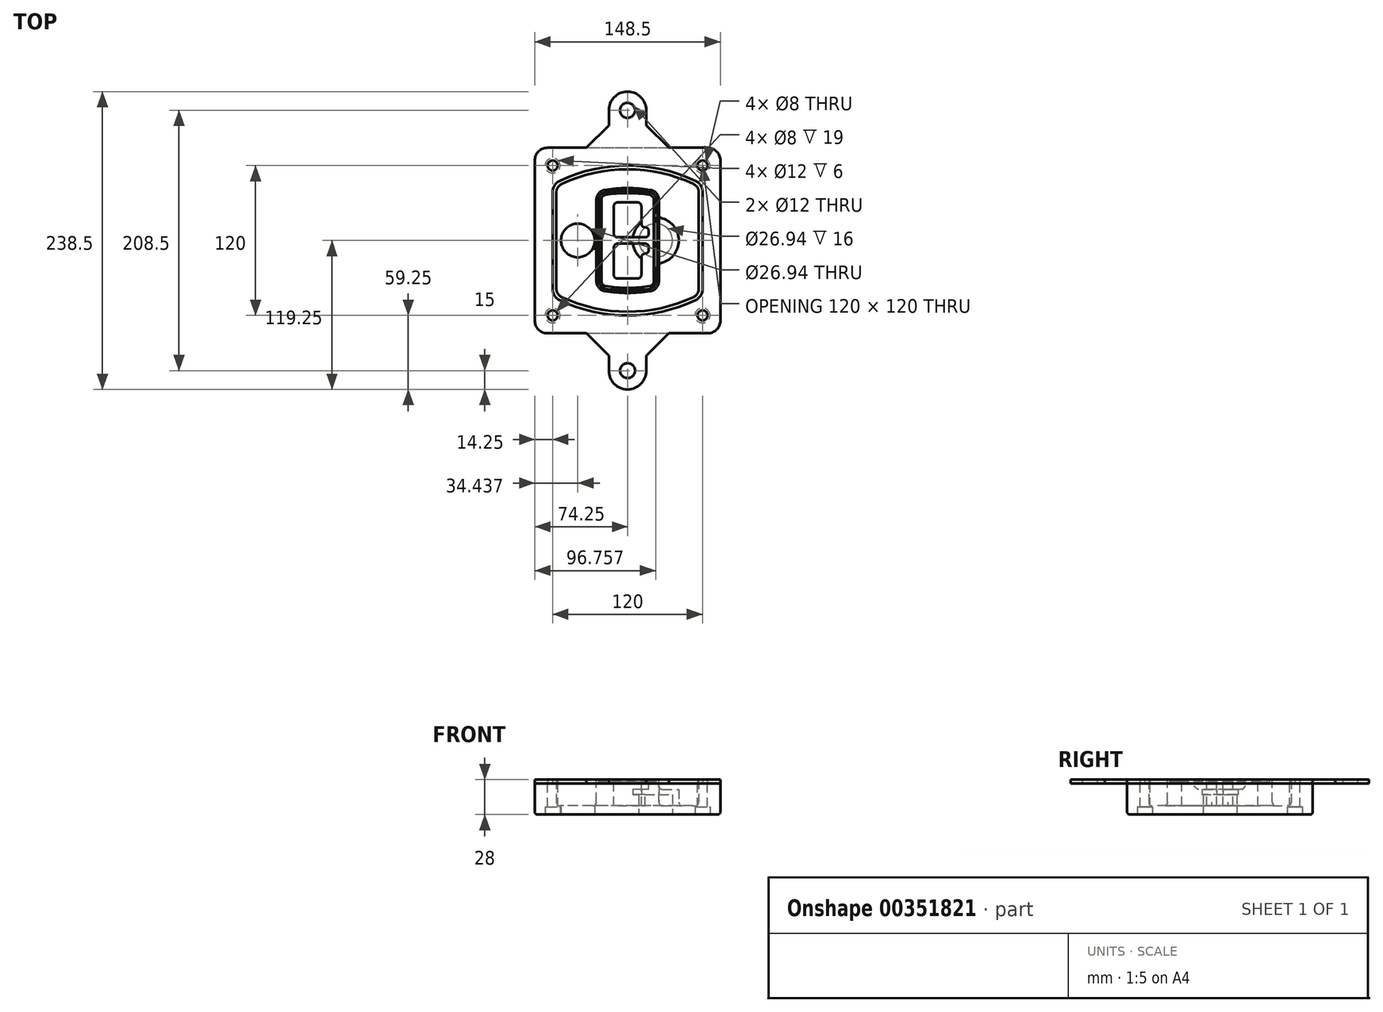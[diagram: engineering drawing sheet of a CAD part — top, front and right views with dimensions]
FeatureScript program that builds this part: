
annotation { "Feature Type Name" : "Feature", "Feature Type Description" : "" }
export const myFeature = defineFeature(function(context is Context, id is Id, definition is map)
    precondition{}
    {
        {
            var Q0;
            Q0=qCreatedBy(makeId("Top.planeOp"),FACE);
            var sketch = newSketch(context, id + "F0", { "sketchPlane" : qUnion([Q0])});
            skPoint(sketch, "E0.rect.middle", {"position": v(0, 0) * mm});
            skLineSegment(sketch, "E1.bottom", {"start": v(-64.25, -74.25) * mm, "end": v(64.25, -74.25) * mm});
            skLineSegment(sketch, "E1.top", {"start": v(-64.25, 74.25) * mm, "end": v(64.25, 74.25) * mm});
            skLineSegment(sketch, "E1.left", {"start": v(-74.25, -64.25) * mm, "end": v(-74.25, 64.25) * mm});
            skLineSegment(sketch, "E1.right", {"start": v(74.25, -64.25) * mm, "end": v(74.25, 64.25) * mm});
            skLineSegment(sketch, "E2", {"start": v(-74.25, 74.25) * mm, "end": v(74.25, -74.25) * mm, "construction": true});
            skLineSegment(sketch, "E3", {"start": v(74.25, 74.25) * mm, "end": v(-74.25, -74.25) * mm, "construction": true});
            skCircle(sketch, "E4", {"center": v(-60, 60) * mm, "radius": 4 * mm});
            skCircle(sketch, "E5", {"center": v(60, 60) * mm, "radius": 4 * mm});
            skCircle(sketch, "E6", {"center": v(60, -60) * mm, "radius": 4 * mm});
            skCircle(sketch, "E7", {"center": v(-60, -60) * mm, "radius": 4 * mm});
            skLineSegment(sketch, "E8", {"start": v(-60, 60) * mm, "end": v(60, 60) * mm, "construction": true});
            skLineSegment(sketch, "E9", {"start": v(60, 60) * mm, "end": v(60, -60) * mm, "construction": true});
            skLineSegment(sketch, "E10", {"start": v(60, -60) * mm, "end": v(-60, -60) * mm, "construction": true});
            skLineSegment(sketch, "E11", {"start": v(-60, -60) * mm, "end": v(-60, 60) * mm, "construction": true});
            skLineSegment(sketch, "E12", {"start": v(-60, 38.83) * mm, "end": v(-60, -38.83) * mm});
            skLineSegment(sketch, "E13", {"start": v(60, 38.83) * mm, "end": v(60, -38.83) * mm});
            skArc(sketch, "E14", {"start": v(54.26, 47.88) * mm, "mid": v(0, 60) * mm, "end": v(-54.26, 47.88) * mm});
            skArc(sketch, "E15", {"start": v(-54.26, -47.88) * mm, "mid": v(0, -60) * mm, "end": v(54.26, -47.88) * mm});
            skLineSegment(sketch, "E16", {"start": v(-60, 0) * mm, "end": v(60, 0) * mm, "construction": true});
            skPoint(sketch, "E17.visualSharp", {"position": v(-60, -45) * mm});
            skArc(sketch, "E17.filletArc", {"start": v(-60, -38.83) * mm, "mid": v(-58.44, -44.2) * mm, "end": v(-54.26, -47.88) * mm});
            skPoint(sketch, "E18.visualSharp", {"position": v(-60, 45) * mm});
            skArc(sketch, "E18.filletArc", {"start": v(-54.26, 47.88) * mm, "mid": v(-58.44, 44.2) * mm, "end": v(-60, 38.83) * mm});
            skPoint(sketch, "E19.visualSharp", {"position": v(60, 45) * mm});
            skArc(sketch, "E19.filletArc", {"start": v(60, 38.83) * mm, "mid": v(58.44, 44.2) * mm, "end": v(54.26, 47.88) * mm});
            skPoint(sketch, "E20.visualSharp", {"position": v(60, -45) * mm});
            skArc(sketch, "E20.filletArc", {"start": v(54.26, -47.88) * mm, "mid": v(58.44, -44.2) * mm, "end": v(60, -38.83) * mm});
            skPoint(sketch, "E21.visualSharp", {"position": v(-74.25, 74.25) * mm});
            skArc(sketch, "E21.filletArc", {"start": v(-64.25, 74.25) * mm, "mid": v(-71.32, 71.32) * mm, "end": v(-74.25, 64.25) * mm});
            skPoint(sketch, "E22.visualSharp", {"position": v(74.25, 74.25) * mm});
            skArc(sketch, "E22.filletArc", {"start": v(74.25, 64.25) * mm, "mid": v(71.32, 71.32) * mm, "end": v(64.25, 74.25) * mm});
            skPoint(sketch, "E23.visualSharp", {"position": v(74.25, -74.25) * mm});
            skArc(sketch, "E23.filletArc", {"start": v(64.25, -74.25) * mm, "mid": v(71.32, -71.32) * mm, "end": v(74.25, -64.25) * mm});
            skPoint(sketch, "E24.visualSharp", {"position": v(-74.25, -74.25) * mm});
            skArc(sketch, "E24.filletArc", {"start": v(-74.25, -64.25) * mm, "mid": v(-71.32, -71.32) * mm, "end": v(-64.25, -74.25) * mm});
            skArc(sketch, "E25.0", {"start": v(57, 38.83) * mm, "mid": v(55.9, 42.58) * mm, "end": v(52.98, 45.17) * mm});
            skLineSegment(sketch, "E25.1", {"start": v(57, 38.83) * mm, "end": v(57, -38.83) * mm});
            skArc(sketch, "E25.2", {"start": v(52.98, -45.17) * mm, "mid": v(55.9, -42.58) * mm, "end": v(57, -38.83) * mm});
            skArc(sketch, "E25.3", {"start": v(-52.98, -45.17) * mm, "mid": v(0, -57) * mm, "end": v(52.98, -45.17) * mm});
            skArc(sketch, "E25.4", {"start": v(-57, -38.83) * mm, "mid": v(-55.9, -42.58) * mm, "end": v(-52.98, -45.17) * mm});
            skArc(sketch, "E25.5", {"start": v(52.98, 45.17) * mm, "mid": v(0, 57) * mm, "end": v(-52.98, 45.17) * mm});
            skLineSegment(sketch, "E25.6", {"start": v(-57, 38.83) * mm, "end": v(-57, -38.83) * mm});
            skArc(sketch, "E25.7", {"start": v(-52.98, 45.17) * mm, "mid": v(-55.9, 42.58) * mm, "end": v(-57, 38.83) * mm});
            skArc(sketch, "E26.0", {"start": v(-55.96, 51.5) * mm, "mid": v(-61.82, 46.33) * mm, "end": v(-64, 38.83) * mm});
            skArc(sketch, "E26.1", {"start": v(55.96, 51.5) * mm, "mid": v(0, 64) * mm, "end": v(-55.96, 51.5) * mm});
            skArc(sketch, "E26.2", {"start": v(64, 38.83) * mm, "mid": v(61.82, 46.33) * mm, "end": v(55.96, 51.5) * mm});
            skLineSegment(sketch, "E26.3", {"start": v(64, 38.83) * mm, "end": v(64, -38.83) * mm});
            skArc(sketch, "E26.4", {"start": v(55.96, -51.5) * mm, "mid": v(61.82, -46.33) * mm, "end": v(64, -38.83) * mm});
            skLineSegment(sketch, "E26.5", {"start": v(-64, 38.83) * mm, "end": v(-64, -38.83) * mm});
            skArc(sketch, "E26.6", {"start": v(-55.96, -51.5) * mm, "mid": v(0, -64) * mm, "end": v(55.96, -51.5) * mm});
            skArc(sketch, "E26.7", {"start": v(-64, -38.83) * mm, "mid": v(-61.82, -46.33) * mm, "end": v(-55.96, -51.5) * mm});
            skSolve(sketch);
        }
        {
            var Q0;
            Q0=makeQuery(id+"F0.imprint","IMPRINT",FACE,{"disambiguationData":[TD([[makeQuery(id+"F0.imprint","IMPRINT",EDGE,{"derivedFrom":sQuery(id+"F0.wireOp",EDGE,"E1.bottom")}),1.0]])]});
            var Q1;
            Q1=makeQuery(id+"F0.imprint","IMPRINT",FACE,{"disambiguationData":[TD([[makeQuery(id+"F0.imprint","IMPRINT",EDGE,{"derivedFrom":sQuery(id+"F0.wireOp",EDGE,"E12")}),1.0]])]});
            var Q2;
            Q2=makeQuery(id+"F0.imprint","IMPRINT",FACE,{"disambiguationData":[TD([[makeQuery(id+"F0.imprint","IMPRINT",EDGE,{"derivedFrom":sQuery(id+"F0.wireOp",EDGE,"E25.0")}),1.0]])]});
            var Q3;
            Q3=makeQuery(id+"F0.imprint","IMPRINT",FACE,{"disambiguationData":[TD([[makeQuery(id+"F0.imprint","IMPRINT",EDGE,{"derivedFrom":sQuery(id+"F0.wireOp",EDGE,"E12")}),-1.0]])]});
            extrude(context, id + "F1", {"entities" : qUnion([Q0, Q1, Q2, Q3]), "oppositeDirection" : true, "depth" : 25 * mm});
        }
        {
            var Q0;
            Q0=makeQuery(id+"F0.imprint","IMPRINT",FACE,{"disambiguationData":[TD([[makeQuery(id+"F0.imprint","IMPRINT",EDGE,{"derivedFrom":sQuery(id+"F0.wireOp",EDGE,"E12")}),1.0]])]});
            extrude(context, id + "F2", {"entities" : qUnion([Q0]), "operationType" : NewBodyOperationType.ADD, "depth" : 3 * mm});
        }
        {
            var Q0;
            Q0=makeQuery(id+"F0.imprint","IMPRINT",FACE,{"disambiguationData":[TD([[makeQuery(id+"F0.imprint","IMPRINT",EDGE,{"derivedFrom":sQuery(id+"F0.wireOp",EDGE,"E25.0")}),1.0]])]});
            extrude(context, id + "F3", {"entities" : qUnion([Q0]), "operationType" : NewBodyOperationType.REMOVE, "oppositeDirection" : true, "depth" : 18 * mm});
        }
        {
            var Q0;
            Q0=makeQuery(id+"F2.opExtrude","CAP_FACE",FACE,{"disambiguationData":[OSD([sQuery(id+"F0.wireOp",EDGE,"E12"),sQuery(id+"F0.wireOp",EDGE,"E13"),sQuery(id+"F0.wireOp",EDGE,"E14"),sQuery(id+"F0.wireOp",EDGE,"E15"),sQuery(id+"F0.wireOp",EDGE,"E17.filletArc"),sQuery(id+"F0.wireOp",EDGE,"E18.filletArc"),sQuery(id+"F0.wireOp",EDGE,"E19.filletArc"),sQuery(id+"F0.wireOp",EDGE,"E20.filletArc"),sQuery(id+"F0.wireOp",EDGE,"E25.0"),sQuery(id+"F0.wireOp",EDGE,"E25.1"),sQuery(id+"F0.wireOp",EDGE,"E25.2"),sQuery(id+"F0.wireOp",EDGE,"E25.3"),sQuery(id+"F0.wireOp",EDGE,"E25.4"),sQuery(id+"F0.wireOp",EDGE,"E25.5"),sQuery(id+"F0.wireOp",EDGE,"E25.6"),sQuery(id+"F0.wireOp",EDGE,"E25.7")])],"isStart":false});
            var sketch = newSketch(context, id + "F4", { "sketchPlane" : qUnion([Q0])});
            skArc(sketch, "E27.0", {"start": v(-18.34, -40.45) * mm, "mid": v(0, -42) * mm, "end": v(18.34, -40.45) * mm});
            skArc(sketch, "E28.0", {"start": v(18.34, 40.45) * mm, "mid": v(0, 42) * mm, "end": v(-18.34, 40.45) * mm});
            skLineSegment(sketch, "E29", {"start": v(-25, 32.57) * mm, "end": v(-25, -32.57) * mm});
            skLineSegment(sketch, "E30", {"start": v(25, 32.57) * mm, "end": v(25, -32.57) * mm});
            skLineSegment(sketch, "E31", {"start": v(-25, 39.1) * mm, "end": v(25, 39.1) * mm, "construction": true});
            skLineSegment(sketch, "E32", {"start": v(-25, -39.1) * mm, "end": v(25, -39.1) * mm, "construction": true});
            skPoint(sketch, "E33.visualSharp", {"position": v(-25, 39.1) * mm});
            skArc(sketch, "E33.filletArc", {"start": v(-18.34, 40.45) * mm, "mid": v(-23.11, 37.73) * mm, "end": v(-25, 32.57) * mm});
            skPoint(sketch, "E34.visualSharp", {"position": v(25, 39.1) * mm});
            skArc(sketch, "E34.filletArc", {"start": v(25, 32.57) * mm, "mid": v(23.11, 37.73) * mm, "end": v(18.34, 40.45) * mm});
            skPoint(sketch, "E35.visualSharp", {"position": v(25, -39.1) * mm});
            skArc(sketch, "E35.filletArc", {"start": v(18.34, -40.45) * mm, "mid": v(23.11, -37.73) * mm, "end": v(25, -32.57) * mm});
            skPoint(sketch, "E36.visualSharp", {"position": v(-25, -39.1) * mm});
            skArc(sketch, "E36.filletArc", {"start": v(-25, -32.57) * mm, "mid": v(-23.11, -37.73) * mm, "end": v(-18.34, -40.45) * mm});
            skArc(sketch, "E37.0", {"start": v(52.98, 45.17) * mm, "mid": v(0, 57) * mm, "end": v(-52.98, 45.17) * mm});
            skArc(sketch, "E37.1", {"start": v(-52.98, 45.17) * mm, "mid": v(-55.9, 42.58) * mm, "end": v(-57, 38.83) * mm});
            skLineSegment(sketch, "E37.2", {"start": v(-57, 38.83) * mm, "end": v(-57, -38.83) * mm});
            skArc(sketch, "E37.3", {"start": v(-57, -38.83) * mm, "mid": v(-55.9, -42.58) * mm, "end": v(-52.98, -45.17) * mm});
            skArc(sketch, "E37.4", {"start": v(-52.98, -45.17) * mm, "mid": v(0, -57) * mm, "end": v(52.98, -45.17) * mm});
            skArc(sketch, "E37.5", {"start": v(52.98, -45.17) * mm, "mid": v(55.9, -42.58) * mm, "end": v(57, -38.83) * mm});
            skLineSegment(sketch, "E37.6", {"start": v(57, 38.83) * mm, "end": v(57, -38.83) * mm});
            skArc(sketch, "E37.7", {"start": v(57, 38.83) * mm, "mid": v(55.9, 42.58) * mm, "end": v(52.98, 45.17) * mm});
            skLineSegment(sketch, "E38.0", {"start": v(23, 32.57) * mm, "end": v(23, -32.57) * mm});
            skArc(sketch, "E38.1", {"start": v(18, -38.48) * mm, "mid": v(21.58, -36.44) * mm, "end": v(23, -32.57) * mm});
            skArc(sketch, "E38.2", {"start": v(-18, -38.48) * mm, "mid": v(0, -40) * mm, "end": v(18, -38.48) * mm});
            skArc(sketch, "E38.3", {"start": v(-23, -32.57) * mm, "mid": v(-21.58, -36.44) * mm, "end": v(-18, -38.48) * mm});
            skLineSegment(sketch, "E38.4", {"start": v(-23, 32.57) * mm, "end": v(-23, -32.57) * mm});
            skArc(sketch, "E38.5", {"start": v(23, 32.57) * mm, "mid": v(21.58, 36.44) * mm, "end": v(18, 38.48) * mm});
            skArc(sketch, "E38.6", {"start": v(-18, 38.48) * mm, "mid": v(-21.58, 36.44) * mm, "end": v(-23, 32.57) * mm});
            skArc(sketch, "E38.7", {"start": v(18, 38.48) * mm, "mid": v(0, 40) * mm, "end": v(-18, 38.48) * mm});
            skArc(sketch, "E39.0", {"start": v(21, 32.57) * mm, "mid": v(20.06, 35.15) * mm, "end": v(17.67, 36.5) * mm});
            skLineSegment(sketch, "E39.1", {"start": v(21, 32.57) * mm, "end": v(21, -32.57) * mm});
            skArc(sketch, "E39.2", {"start": v(17.67, -36.5) * mm, "mid": v(20.06, -35.15) * mm, "end": v(21, -32.57) * mm});
            skArc(sketch, "E39.3", {"start": v(-17.67, -36.5) * mm, "mid": v(0, -38) * mm, "end": v(17.67, -36.5) * mm});
            skArc(sketch, "E39.4", {"start": v(-21, -32.57) * mm, "mid": v(-20.06, -35.15) * mm, "end": v(-17.67, -36.5) * mm});
            skArc(sketch, "E39.5", {"start": v(17.67, 36.5) * mm, "mid": v(0, 38) * mm, "end": v(-17.67, 36.5) * mm});
            skLineSegment(sketch, "E39.6", {"start": v(-21, 32.57) * mm, "end": v(-21, -32.57) * mm});
            skArc(sketch, "E39.7", {"start": v(-17.67, 36.5) * mm, "mid": v(-20.06, 35.15) * mm, "end": v(-21, 32.57) * mm});
            skLineSegment(sketch, "E40", {"start": v(-25, 0) * mm, "end": v(25, 0) * mm, "construction": true});
            skLineSegment(sketch, "E41", {"start": v(-11, 5.5) * mm, "end": v(-11, 27.5) * mm});
            skLineSegment(sketch, "E42", {"start": v(-8, 30.5) * mm, "end": v(8, 30.5) * mm});
            skLineSegment(sketch, "E43", {"start": v(11, 27.5) * mm, "end": v(11, 13.5) * mm});
            skLineSegment(sketch, "E44", {"start": v(14, 10.5) * mm, "end": v(14, 10.5) * mm});
            skLineSegment(sketch, "E45", {"start": v(17, 7.5) * mm, "end": v(17, 5.5) * mm});
            skLineSegment(sketch, "E46", {"start": v(14, 2.5) * mm, "end": v(-8, 2.5) * mm});
            skPoint(sketch, "E47.visualSharp", {"position": v(-11, 30.5) * mm});
            skArc(sketch, "E47.filletArc", {"start": v(-8, 30.5) * mm, "mid": v(-10.12, 29.62) * mm, "end": v(-11, 27.5) * mm});
            skPoint(sketch, "E48.visualSharp", {"position": v(11, 30.5) * mm});
            skArc(sketch, "E48.filletArc", {"start": v(11, 27.5) * mm, "mid": v(10.12, 29.62) * mm, "end": v(8, 30.5) * mm});
            skPoint(sketch, "E49.visualSharp", {"position": v(11, 10.5) * mm});
            skArc(sketch, "E49.filletArc", {"start": v(11, 13.5) * mm, "mid": v(11.88, 11.38) * mm, "end": v(14, 10.5) * mm});
            skPoint(sketch, "E50.visualSharp", {"position": v(17, 10.5) * mm});
            skArc(sketch, "E50.filletArc", {"start": v(17, 7.5) * mm, "mid": v(16.12, 9.62) * mm, "end": v(14, 10.5) * mm});
            skPoint(sketch, "E51.visualSharp", {"position": v(17, 2.5) * mm});
            skArc(sketch, "E51.filletArc", {"start": v(14, 2.5) * mm, "mid": v(16.12, 3.38) * mm, "end": v(17, 5.5) * mm});
            skPoint(sketch, "E52.visualSharp", {"position": v(-11, 2.5) * mm});
            skArc(sketch, "E52.filletArc", {"start": v(-11, 5.5) * mm, "mid": v(-10.12, 3.38) * mm, "end": v(-8, 2.5) * mm});
            skLineSegment(sketch, "E53.0.MirrorCS", {"start": v(14, -2.5) * mm, "end": v(-8, -2.5) * mm});
            skArc(sketch, "E54.0.MirrorCS", {"start": v(-11, -5.5) * mm, "mid": v(-10.12, -3.38) * mm, "end": v(-8, -2.5) * mm});
            skLineSegment(sketch, "E55.0.MirrorCS", {"start": v(-11, -5.5) * mm, "end": v(-11, -27.5) * mm});
            skArc(sketch, "E56.0.MirrorCS", {"start": v(-8, -30.5) * mm, "mid": v(-10.12, -29.62) * mm, "end": v(-11, -27.5) * mm});
            skLineSegment(sketch, "E57.0.MirrorCS", {"start": v(-8, -30.5) * mm, "end": v(8, -30.5) * mm});
            skArc(sketch, "E58.0.MirrorCS", {"start": v(11, -27.5) * mm, "mid": v(10.12, -29.62) * mm, "end": v(8, -30.5) * mm});
            skLineSegment(sketch, "E59.0.MirrorCS", {"start": v(11, -27.5) * mm, "end": v(11, -13.5) * mm});
            skArc(sketch, "E60.0.MirrorCS", {"start": v(11, -13.5) * mm, "mid": v(11.88, -11.38) * mm, "end": v(14, -10.5) * mm});
            skArc(sketch, "E61.0.MirrorCS", {"start": v(17, -7.5) * mm, "mid": v(16.12, -9.62) * mm, "end": v(14, -10.5) * mm});
            skLineSegment(sketch, "E62.0.MirrorCS", {"start": v(17, -7.5) * mm, "end": v(17, -5.5) * mm});
            skArc(sketch, "E63.0.MirrorCS", {"start": v(14, -2.5) * mm, "mid": v(16.12, -3.38) * mm, "end": v(17, -5.5) * mm});
            skSolve(sketch);
        }
        {
            var Q0;
            Q0=makeQuery(id+"F4.imprint","IMPRINT",FACE,{"disambiguationData":[TD([[makeQuery(id+"F4.imprint","IMPRINT",EDGE,{"derivedFrom":sQuery(id+"F4.wireOp",EDGE,"E27.0")}),1.0]])]});
            var Q1;
            Q1=makeQuery(id+"F4.imprint","IMPRINT",FACE,{"disambiguationData":[TD([[makeQuery(id+"F4.imprint","IMPRINT",EDGE,{"derivedFrom":sQuery(id+"F4.wireOp",EDGE,"E38.0")}),-1.0]])]});
            var Q2;
            Q2=makeQuery(id+"F4.imprint","IMPRINT",FACE,{"disambiguationData":[TD([[makeQuery(id+"F4.imprint","IMPRINT",EDGE,{"derivedFrom":sQuery(id+"F4.wireOp",EDGE,"E39.0")}),1.0]])]});
            extrude(context, id + "F5", {"entities" : qUnion([Q0, Q1, Q2]), "operationType" : NewBodyOperationType.ADD, "endBound" : BoundingType.UP_TO_NEXT, "oppositeDirection" : true, "depth" : 25 * mm});
        }
        {
            var Q0;
            Q0=makeQuery(id+"F4.imprint","IMPRINT",FACE,{"disambiguationData":[TD([[makeQuery(id+"F4.imprint","IMPRINT",EDGE,{"derivedFrom":sQuery(id+"F4.wireOp",EDGE,"E38.0")}),-1.0]])]});
            extrude(context, id + "F6", {"entities" : qUnion([Q0]), "operationType" : NewBodyOperationType.REMOVE, "oppositeDirection" : true, "depth" : 2 * mm});
        }
        {
            var Q0;
            Q0=makeQuery(id+"F1.opExtrude","CAP_FACE",FACE,{"disambiguationData":[OSD([sQuery(id+"F0.wireOp",EDGE,"E1.bottom"),sQuery(id+"F0.wireOp",EDGE,"E1.top"),sQuery(id+"F0.wireOp",EDGE,"E1.left"),sQuery(id+"F0.wireOp",EDGE,"E1.right"),sQuery(id+"F0.wireOp",EDGE,"E4"),sQuery(id+"F0.wireOp",EDGE,"E5"),sQuery(id+"F0.wireOp",EDGE,"E6"),sQuery(id+"F0.wireOp",EDGE,"E7"),sQuery(id+"F0.wireOp",EDGE,"E21.filletArc"),sQuery(id+"F0.wireOp",EDGE,"E22.filletArc"),sQuery(id+"F0.wireOp",EDGE,"E23.filletArc"),sQuery(id+"F0.wireOp",EDGE,"E24.filletArc")])],"isStart":false});
            var sketch = newSketch(context, id + "F7", { "sketchPlane" : qUnion([Q0])});
            skCircle(sketch, "E64", {"center": v(22.5, 0) * mm, "radius": 13.47 * mm});
            skCircle(sketch, "E65", {"center": v(-39.81, 0) * mm, "radius": 13.47 * mm});
            skLineSegment(sketch, "E66", {"start": v(74.25, 0) * mm, "end": v(-74.25, 0) * mm});
            skCircle(sketch, "E67", {"center": v(22.5, 0) * mm, "radius": 18.47 * mm});
            skCircle(sketch, "E68", {"center": v(60, -60) * mm, "radius": 6 * mm});
            skCircle(sketch, "E69", {"center": v(-60, -60) * mm, "radius": 6 * mm});
            skCircle(sketch, "E70", {"center": v(-60, 60) * mm, "radius": 6 * mm});
            skCircle(sketch, "E71", {"center": v(60, 60) * mm, "radius": 6 * mm});
            skSolve(sketch);
        }
        {
            var Q0;
            {var subQ1=sQuery(id+"F7.wireOp",EDGE,"E66");var subQ4=sQuery(id+"F7.wireOp",EDGE,"E64");var subQ6=makeQuery(id+"F7.imprint","INTERSECT",VERTEX,{"disambiguationData":[OD(0.0)],"derivedFrom":[subQ4,subQ1]});Q0=makeQuery(id+"F7.imprint","IMPRINT",FACE,{"disambiguationData":[TD([[makeQuery(id+"F7.imprint","IMPRINT",EDGE,{"disambiguationData":[TD([[subQ6,-1.0]])],"derivedFrom":subQ4}),-1.0]])]});}
            var Q1;
            {var subQ0=sQuery(id+"F7.wireOp",EDGE,"E66");var subQ1=sQuery(id+"F7.wireOp",EDGE,"E64");var subQ3=makeQuery(id+"F7.imprint","INTERSECT",VERTEX,{"disambiguationData":[OD(0.0)],"derivedFrom":[subQ1,subQ0]});Q1=makeQuery(id+"F7.imprint","IMPRINT",FACE,{"disambiguationData":[TD([[makeQuery(id+"F7.imprint","IMPRINT",EDGE,{"disambiguationData":[TD([[subQ3,-1.0]])],"derivedFrom":subQ1}),1.0]])]});}
            var Q2;
            {var subQ0=sQuery(id+"F7.wireOp",EDGE,"E66");var subQ1=sQuery(id+"F7.wireOp",EDGE,"E64");var subQ3=makeQuery(id+"F7.imprint","INTERSECT",VERTEX,{"disambiguationData":[OD(0.0)],"derivedFrom":[subQ1,subQ0]});Q2=makeQuery(id+"F7.imprint","IMPRINT",FACE,{"disambiguationData":[TD([[makeQuery(id+"F7.imprint","IMPRINT",EDGE,{"disambiguationData":[TD([[subQ3,1.0]])],"derivedFrom":subQ1}),1.0]])]});}
            var Q3;
            {var subQ1=sQuery(id+"F7.wireOp",EDGE,"E66");var subQ4=sQuery(id+"F7.wireOp",EDGE,"E64");var subQ6=makeQuery(id+"F7.imprint","INTERSECT",VERTEX,{"disambiguationData":[OD(0.0)],"derivedFrom":[subQ4,subQ1]});Q3=makeQuery(id+"F7.imprint","IMPRINT",FACE,{"disambiguationData":[TD([[makeQuery(id+"F7.imprint","IMPRINT",EDGE,{"disambiguationData":[TD([[subQ6,1.0]])],"derivedFrom":subQ4}),-1.0]])]});}
            extrude(context, id + "F8", {"entities" : qUnion([Q0, Q1, Q2, Q3]), "operationType" : NewBodyOperationType.ADD, "oppositeDirection" : true, "depth" : 20 * mm});
        }
        {
            var Q0;
            {var subQ0=sQuery(id+"F7.wireOp",EDGE,"E66");var subQ1=sQuery(id+"F7.wireOp",EDGE,"E64");var subQ3=makeQuery(id+"F7.imprint","INTERSECT",VERTEX,{"disambiguationData":[OD(0.0)],"derivedFrom":[subQ1,subQ0]});Q0=makeQuery(id+"F7.imprint","IMPRINT",FACE,{"disambiguationData":[TD([[makeQuery(id+"F7.imprint","IMPRINT",EDGE,{"disambiguationData":[TD([[subQ3,-1.0]])],"derivedFrom":subQ1}),1.0]])]});}
            var Q1;
            {var subQ0=sQuery(id+"F7.wireOp",EDGE,"E66");var subQ1=sQuery(id+"F7.wireOp",EDGE,"E64");var subQ3=makeQuery(id+"F7.imprint","INTERSECT",VERTEX,{"disambiguationData":[OD(0.0)],"derivedFrom":[subQ1,subQ0]});Q1=makeQuery(id+"F7.imprint","IMPRINT",FACE,{"disambiguationData":[TD([[makeQuery(id+"F7.imprint","IMPRINT",EDGE,{"disambiguationData":[TD([[subQ3,1.0]])],"derivedFrom":subQ1}),1.0]])]});}
            extrude(context, id + "F9", {"entities" : qUnion([Q0, Q1]), "operationType" : NewBodyOperationType.REMOVE, "oppositeDirection" : true, "depth" : 16 * mm});
        }
        {
            var Q0;
            {var subQ0=sQuery(id+"F7.wireOp",EDGE,"E66");var subQ1=sQuery(id+"F7.wireOp",EDGE,"E65");var subQ3=makeQuery(id+"F7.imprint","INTERSECT",VERTEX,{"disambiguationData":[OD(0.0)],"derivedFrom":[subQ1,subQ0]});Q0=makeQuery(id+"F7.imprint","IMPRINT",FACE,{"disambiguationData":[TD([[makeQuery(id+"F7.imprint","IMPRINT",EDGE,{"disambiguationData":[TD([[subQ3,-1.0]])],"derivedFrom":subQ1}),1.0]])]});}
            var Q1;
            {var subQ0=sQuery(id+"F7.wireOp",EDGE,"E66");var subQ1=sQuery(id+"F7.wireOp",EDGE,"E65");var subQ3=makeQuery(id+"F7.imprint","INTERSECT",VERTEX,{"disambiguationData":[OD(0.0)],"derivedFrom":[subQ1,subQ0]});Q1=makeQuery(id+"F7.imprint","IMPRINT",FACE,{"disambiguationData":[TD([[makeQuery(id+"F7.imprint","IMPRINT",EDGE,{"disambiguationData":[TD([[subQ3,1.0]])],"derivedFrom":subQ1}),1.0]])]});}
            extrude(context, id + "F10", {"entities" : qUnion([Q0, Q1]), "operationType" : NewBodyOperationType.REMOVE, "oppositeDirection" : true, "depth" : 25 * mm});
        }
        {
            var Q0;
            Q0=makeQuery(id+"F7.imprint","IMPRINT",FACE,{"disambiguationData":[TD([[makeQuery(id+"F7.imprint","IMPRINT",EDGE,{"derivedFrom":sQuery(id+"F7.wireOp",EDGE,"E68")}),1.0]])]});
            var Q1;
            Q1=makeQuery(id+"F7.imprint","IMPRINT",FACE,{"disambiguationData":[TD([[makeQuery(id+"F7.imprint","IMPRINT",EDGE,{"derivedFrom":makeQuery(id+"F1.opExtrude","CAP_EDGE",EDGE,{"disambiguationData":[OSD([sQuery(id+"F0.wireOp",EDGE,"E5")])],"isStart":false})}),-1.0]])]});
            var Q2;
            Q2=makeQuery(id+"F7.imprint","IMPRINT",FACE,{"disambiguationData":[TD([[makeQuery(id+"F7.imprint","IMPRINT",EDGE,{"derivedFrom":sQuery(id+"F7.wireOp",EDGE,"E69")}),1.0]])]});
            var Q3;
            Q3=makeQuery(id+"F7.imprint","IMPRINT",FACE,{"disambiguationData":[TD([[makeQuery(id+"F7.imprint","IMPRINT",EDGE,{"derivedFrom":makeQuery(id+"F1.opExtrude","CAP_EDGE",EDGE,{"disambiguationData":[OSD([sQuery(id+"F0.wireOp",EDGE,"E4")])],"isStart":false})}),-1.0]])]});
            var Q4;
            Q4=makeQuery(id+"F7.imprint","IMPRINT",FACE,{"disambiguationData":[TD([[makeQuery(id+"F7.imprint","IMPRINT",EDGE,{"derivedFrom":sQuery(id+"F7.wireOp",EDGE,"E70")}),1.0]])]});
            var Q5;
            Q5=makeQuery(id+"F7.imprint","IMPRINT",FACE,{"disambiguationData":[TD([[makeQuery(id+"F7.imprint","IMPRINT",EDGE,{"derivedFrom":makeQuery(id+"F1.opExtrude","CAP_EDGE",EDGE,{"disambiguationData":[OSD([sQuery(id+"F0.wireOp",EDGE,"E7")])],"isStart":false})}),-1.0]])]});
            var Q6;
            Q6=makeQuery(id+"F7.imprint","IMPRINT",FACE,{"disambiguationData":[TD([[makeQuery(id+"F7.imprint","IMPRINT",EDGE,{"derivedFrom":sQuery(id+"F7.wireOp",EDGE,"E71")}),1.0]])]});
            var Q7;
            Q7=makeQuery(id+"F7.imprint","IMPRINT",FACE,{"disambiguationData":[TD([[makeQuery(id+"F7.imprint","IMPRINT",EDGE,{"derivedFrom":makeQuery(id+"F1.opExtrude","CAP_EDGE",EDGE,{"disambiguationData":[OSD([sQuery(id+"F0.wireOp",EDGE,"E6")])],"isStart":false})}),-1.0]])]});
            extrude(context, id + "F11", {"entities" : qUnion([Q0, Q1, Q2, Q3, Q4, Q5, Q6, Q7]), "operationType" : NewBodyOperationType.REMOVE, "oppositeDirection" : true, "depth" : 6 * mm});
        }
        {
            var Q0;
            Q0=makeQuery(id+"F9.boolean.opBoolean","COPY",FACE,{"derivedFrom":makeQuery(id+"F9.opExtrude","CAP_FACE",FACE,{"disambiguationData":[OSD([sQuery(id+"F7.wireOp",EDGE,"E64")])],"isStart":false})});
            var sketch = newSketch(context, id + "F12", { "sketchPlane" : qUnion([Q0])});
            skArc(sketch, "E72.0", {"start": v(11, 14.45) * mm, "mid": v(6.45, 9.13) * mm, "end": v(4.2, 2.5) * mm});
            skArc(sketch, "E72.1", {"start": v(4.2, -2.5) * mm, "mid": v(6.45, -9.13) * mm, "end": v(11, -14.45) * mm});
            skLineSegment(sketch, "E73", {"start": v(4.2, -2.5) * mm, "end": v(14, -2.5) * mm});
            skLineSegment(sketch, "E74.0", {"start": v(14, 2.5) * mm, "end": v(4.2, 2.5) * mm});
            skArc(sketch, "E74.1", {"start": v(14, 2.5) * mm, "mid": v(16.12, 3.38) * mm, "end": v(17, 5.5) * mm});
            skLineSegment(sketch, "E74.2", {"start": v(17, 7.5) * mm, "end": v(17, 5.5) * mm});
            skArc(sketch, "E74.3", {"start": v(17, 7.5) * mm, "mid": v(16.12, 9.62) * mm, "end": v(14, 10.5) * mm});
            skArc(sketch, "E74.4", {"start": v(11, 13.5) * mm, "mid": v(11.88, 11.38) * mm, "end": v(14, 10.5) * mm});
            skLineSegment(sketch, "E74.5", {"start": v(11, 14.45) * mm, "end": v(11, 13.5) * mm});
            skLineSegment(sketch, "E74.7", {"start": v(14, -2.5) * mm, "end": v(4.2, -2.5) * mm});
            skArc(sketch, "E74.8", {"start": v(14, -2.5) * mm, "mid": v(16.12, -3.38) * mm, "end": v(17, -5.5) * mm});
            skLineSegment(sketch, "E74.9", {"start": v(17, -7.5) * mm, "end": v(17, -5.5) * mm});
            skArc(sketch, "E74.10", {"start": v(17, -7.5) * mm, "mid": v(16.12, -9.62) * mm, "end": v(14, -10.5) * mm});
            skArc(sketch, "E74.11", {"start": v(11, -13.5) * mm, "mid": v(11.88, -11.38) * mm, "end": v(14, -10.5) * mm});
            skLineSegment(sketch, "E74.12", {"start": v(11, -14.45) * mm, "end": v(11, -13.5) * mm});
            skPoint(sketch, "E75.orphan", {"position": v(11, -27.5) * mm});
            skPoint(sketch, "E76.orphan", {"position": v(-8, -2.5) * mm});
            skPoint(sketch, "E77.orphan", {"position": v(-8, 2.5) * mm});
            skPoint(sketch, "E78.orphan", {"position": v(11, 27.5) * mm});
            skSolve(sketch);
        }
        {
            var Q0;
            {var subQ7=sQuery(id+"F12.wireOp",EDGE,"E72.0");var subQ14=sQuery(id+"F12.wireOp",EDGE,"E72.1");var subQ16=sQuery(id+"F12.wireOp",EDGE,"E74.1");var subQ18=sQuery(id+"F12.wireOp",EDGE,"E74.8");Q0=qUnion([makeQuery(id+"F12.imprint","IMPRINT",FACE,{"disambiguationData":[TD([[makeQuery(id+"F12.imprint","IMPRINT",EDGE,{"derivedFrom":subQ7}),1.0]])]}),makeQuery(id+"F12.imprint","IMPRINT",FACE,{"disambiguationData":[TD([[makeQuery(id+"F12.imprint","IMPRINT",EDGE,{"derivedFrom":subQ14}),1.0]])]}),makeQuery(id+"F12.imprint","IMPRINT",FACE,{"disambiguationData":[TD([[makeQuery(id+"F12.imprint","IMPRINT",EDGE,{"derivedFrom":subQ16}),1.0]])]}),makeQuery(id+"F12.imprint","IMPRINT",FACE,{"disambiguationData":[TD([[makeQuery(id+"F12.imprint","IMPRINT",EDGE,{"derivedFrom":subQ18}),-1.0]])]})]);}
            var Q1;
            Q1=makeQuery(id+"F5.boolean.opBoolean","SPLIT",FACE,{"disambiguationData":[TD([makeQuery(id+"F5.opExtrude","SWEPT_FACE",FACE,{"disambiguationData":[OSD([sQuery(id+"F4.wireOp",EDGE,"E41")])]})])],"derivedFrom":makeQuery(id+"F3.boolean.opBoolean","COPY",FACE,{"derivedFrom":makeQuery(id+"F3.opExtrude","CAP_FACE",FACE,{"disambiguationData":[OSD([sQuery(id+"F0.wireOp",EDGE,"E25.0"),sQuery(id+"F0.wireOp",EDGE,"E25.1"),sQuery(id+"F0.wireOp",EDGE,"E25.2"),sQuery(id+"F0.wireOp",EDGE,"E25.3"),sQuery(id+"F0.wireOp",EDGE,"E25.4"),sQuery(id+"F0.wireOp",EDGE,"E25.5"),sQuery(id+"F0.wireOp",EDGE,"E25.6"),sQuery(id+"F0.wireOp",EDGE,"E25.7")])],"isStart":false})})});
            extrude(context, id + "F13", {"entities" : qUnion([Q0]), "operationType" : NewBodyOperationType.REMOVE, "endBound" : BoundingType.UP_TO_SURFACE, "endBoundEntityFace" : qUnion([Q1]), "depth" : 25 * mm});
        }
        {
            var Q0;
            Q0=makeQuery(id+"F3.boolean.opBoolean","COPY",EDGE,{"derivedFrom":makeQuery(id+"F3.opExtrude","CAP_EDGE",EDGE,{"disambiguationData":[OSD([sQuery(id+"F0.wireOp",EDGE,"E25.6")])],"isStart":false})});
            var Q1;
            Q1=makeQuery(id+"F8.boolean.opBoolean","INTERSECT",EDGE,{"derivedFrom":[makeQuery(id+"F5.opExtrude","SWEPT_FACE",FACE,{"disambiguationData":[OSD([sQuery(id+"F4.wireOp",EDGE,"E30")])]}),makeQuery(id+"F8.opExtrude","CAP_FACE",FACE,{"disambiguationData":[OSD([sQuery(id+"F7.wireOp",EDGE,"E67")])],"isStart":false})]});
            var Q2;
            Q2=makeQuery(id+"F8.boolean.opBoolean","INTERSECT",EDGE,{"disambiguationData":[OD(1.0)],"derivedFrom":[makeQuery(id+"F5.opExtrude","SWEPT_FACE",FACE,{"disambiguationData":[OSD([sQuery(id+"F4.wireOp",EDGE,"E30")])]}),makeQuery(id+"F8.opExtrude","SWEPT_FACE",FACE,{"disambiguationData":[OSD([sQuery(id+"F7.wireOp",EDGE,"E67")])]})]});
            var Q3;
            {var subQ0=sQuery(id+"F4.wireOp",EDGE,"E30");Q3=makeQuery(id+"F8.boolean.opBoolean","SPLIT",EDGE,{"disambiguationData":[TD([makeQuery(id+"F5.opExtrude","SWEPT_FACE",FACE,{"disambiguationData":[OSD([sQuery(id+"F4.wireOp",EDGE,"E35.filletArc")])]})])],"derivedFrom":makeQuery(id+"F5.opExtrude","CAP_EDGE",EDGE,{"disambiguationData":[OSD([subQ0])],"isStart":false})});}
            var Q4;
            {var subQ0=sQuery(id+"F0.wireOp",EDGE,"E25.7");var subQ1=sQuery(id+"F0.wireOp",EDGE,"E25.1");var subQ2=sQuery(id+"F0.wireOp",EDGE,"E25.6");var subQ3=sQuery(id+"F0.wireOp",EDGE,"E25.5");var subQ4=sQuery(id+"F0.wireOp",EDGE,"E25.4");var subQ5=sQuery(id+"F0.wireOp",EDGE,"E25.0");var subQ6=sQuery(id+"F0.wireOp",EDGE,"E25.2");var subQ7=sQuery(id+"F0.wireOp",EDGE,"E25.3");Q4=makeQuery(id+"F8.boolean.opBoolean","INTERSECT",EDGE,{"derivedFrom":[makeQuery(id+"F5.boolean.opBoolean","SPLIT",FACE,{"disambiguationData":[TD([makeQuery(id+"F2.opExtrude","SWEPT_FACE",FACE,{"disambiguationData":[OSD([subQ5])]})])],"derivedFrom":makeQuery(id+"F3.boolean.opBoolean","COPY",FACE,{"derivedFrom":makeQuery(id+"F3.opExtrude","CAP_FACE",FACE,{"disambiguationData":[OSD([subQ5,subQ1,subQ6,subQ7,subQ4,subQ3,subQ2,subQ0])],"isStart":false})})}),makeQuery(id+"F8.opExtrude","SWEPT_FACE",FACE,{"disambiguationData":[OSD([sQuery(id+"F7.wireOp",EDGE,"E67")])]})]});}
            var Q5;
            Q5=makeQuery(id+"F8.boolean.opBoolean","INTERSECT",EDGE,{"disambiguationData":[OD(0.0)],"derivedFrom":[makeQuery(id+"F5.opExtrude","SWEPT_FACE",FACE,{"disambiguationData":[OSD([sQuery(id+"F4.wireOp",EDGE,"E30")])]}),makeQuery(id+"F8.opExtrude","SWEPT_FACE",FACE,{"disambiguationData":[OSD([sQuery(id+"F7.wireOp",EDGE,"E67")])]})]});
            fillet(context, id + "F14", {"entities" : qUnion([Q0, Q1, Q2, Q3, Q4, Q5]), "radius" : 3 * mm, "tangentPropagation" : true, "allowEdgeOverflow" : false});
        }
        {
            var Q0;
            Q0=makeQuery(id+"F1.opExtrude","CAP_EDGE",EDGE,{"disambiguationData":[OSD([sQuery(id+"F0.wireOp",EDGE,"E1.bottom")])],"isStart":false});
            fillet(context, id + "F15", {"entities" : qUnion([Q0]), "radius" : 2 * mm, "tangentPropagation" : true, "allowEdgeOverflow" : false});
        }
        {
            var Q0;
            {var subQ0=sQuery(id+"F0.wireOp",EDGE,"E21.filletArc");var subQ1=sQuery(id+"F0.wireOp",EDGE,"E7");var subQ2=sQuery(id+"F0.wireOp",EDGE,"E6");var subQ3=sQuery(id+"F0.wireOp",EDGE,"E5");var subQ4=sQuery(id+"F0.wireOp",EDGE,"E4");var subQ5=sQuery(id+"F0.wireOp",EDGE,"E22.filletArc");var subQ6=sQuery(id+"F0.wireOp",EDGE,"E1.bottom");var subQ7=sQuery(id+"F0.wireOp",EDGE,"E1.right");var subQ8=sQuery(id+"F0.wireOp",EDGE,"E1.top");var subQ9=sQuery(id+"F0.wireOp",EDGE,"E1.left");var subQ10=sQuery(id+"F0.wireOp",EDGE,"E23.filletArc");var subQ11=sQuery(id+"F0.wireOp",EDGE,"E24.filletArc");Q0=makeQuery(id+"F2.boolean.opBoolean","SPLIT",FACE,{"disambiguationData":[TD([makeQuery(id+"F1.opExtrude","SWEPT_FACE",FACE,{"disambiguationData":[OSD([subQ6])]})])],"derivedFrom":makeQuery(id+"F1.opExtrude","CAP_FACE",FACE,{"disambiguationData":[OSD([subQ6,subQ8,subQ9,subQ7,subQ4,subQ3,subQ2,subQ1,subQ0,subQ5,subQ10,subQ11])],"isStart":true})});}
            var sketch = newSketch(context, id + "F16", { "sketchPlane" : qUnion([Q0])});
            skLineSegment(sketch, "E79.0", {"start": v(-64.25, 74.25) * mm, "end": v(64.25, 74.25) * mm});
            skArc(sketch, "E79.1", {"start": v(54.26, 47.88) * mm, "mid": v(0, 60) * mm, "end": v(-54.26, 47.88) * mm});
            skCircle(sketch, "E79.2", {"center": v(-60, 60) * mm, "radius": 4 * mm});
            skArc(sketch, "E79.3", {"start": v(-64.25, 74.25) * mm, "mid": v(-71.32, 71.32) * mm, "end": v(-74.25, 64.25) * mm});
            skLineSegment(sketch, "E79.4", {"start": v(-74.25, -64.25) * mm, "end": v(-74.25, 64.25) * mm});
            skLineSegment(sketch, "E79.5", {"start": v(-60, 38.83) * mm, "end": v(-60, -38.83) * mm});
            skArc(sketch, "E79.6", {"start": v(-54.26, 47.88) * mm, "mid": v(-58.44, 44.2) * mm, "end": v(-60, 38.83) * mm});
            skCircle(sketch, "E79.7", {"center": v(60, 60) * mm, "radius": 4 * mm});
            skArc(sketch, "E79.8", {"start": v(74.25, 64.25) * mm, "mid": v(71.32, 71.32) * mm, "end": v(64.25, 74.25) * mm});
            skArc(sketch, "E79.9", {"start": v(60, 38.83) * mm, "mid": v(58.44, 44.2) * mm, "end": v(54.26, 47.88) * mm});
            skLineSegment(sketch, "E79.10", {"start": v(60, 38.83) * mm, "end": v(60, -38.83) * mm});
            skLineSegment(sketch, "E79.11", {"start": v(74.25, -64.25) * mm, "end": v(74.25, 64.25) * mm});
            skCircle(sketch, "E79.12", {"center": v(60, -60) * mm, "radius": 4 * mm});
            skArc(sketch, "E79.13", {"start": v(64.25, -74.25) * mm, "mid": v(71.32, -71.32) * mm, "end": v(74.25, -64.25) * mm});
            skLineSegment(sketch, "E79.14", {"start": v(-64.25, -74.25) * mm, "end": v(64.25, -74.25) * mm});
            skArc(sketch, "E79.15", {"start": v(-54.26, -47.88) * mm, "mid": v(0, -60) * mm, "end": v(54.26, -47.88) * mm});
            skArc(sketch, "E79.16", {"start": v(54.26, -47.88) * mm, "mid": v(58.44, -44.2) * mm, "end": v(60, -38.83) * mm});
            skArc(sketch, "E79.17", {"start": v(-60, -38.83) * mm, "mid": v(-58.44, -44.2) * mm, "end": v(-54.26, -47.88) * mm});
            skCircle(sketch, "E79.18", {"center": v(-60, -60) * mm, "radius": 4 * mm});
            skArc(sketch, "E79.19", {"start": v(-74.25, -64.25) * mm, "mid": v(-71.32, -71.32) * mm, "end": v(-64.25, -74.25) * mm});
            skLineSegment(sketch, "E80", {"start": v(0, 74.25) * mm, "end": v(0, 104.25) * mm, "construction": true});
            skCircle(sketch, "E81", {"center": v(0, 104.25) * mm, "radius": 6 * mm});
            skLineSegment(sketch, "E82", {"start": v(-33, 74.25) * mm, "end": v(-15, 92.25) * mm});
            skLineSegment(sketch, "E83", {"start": v(-15, 92.25) * mm, "end": v(-15, 104.25) * mm});
            skArc(sketch, "E84", {"start": v(-15, 104.25) * mm, "mid": v(0, 119.25) * mm, "end": v(15, 104.25) * mm});
            skLineSegment(sketch, "E85", {"start": v(15, 104.25) * mm, "end": v(15, 92.25) * mm});
            skLineSegment(sketch, "E86", {"start": v(15, 92.25) * mm, "end": v(33, 74.25) * mm});
            skLineSegment(sketch, "E87", {"start": v(-74.25, 0) * mm, "end": v(74.25, 0) * mm, "construction": true});
            skLineSegment(sketch, "E88.MirrorCS", {"start": v(-33, -74.25) * mm, "end": v(-15, -92.25) * mm});
            skLineSegment(sketch, "E89.MirrorCS", {"start": v(-15, -92.25) * mm, "end": v(-15, -104.25) * mm});
            skLineSegment(sketch, "E90.MirrorCS", {"start": v(15, -92.25) * mm, "end": v(33, -74.25) * mm});
            skArc(sketch, "E91.MirrorCS", {"start": v(-15, -104.25) * mm, "mid": v(0, -119.25) * mm, "end": v(15, -104.25) * mm});
            skLineSegment(sketch, "E92.MirrorCS", {"start": v(15, -104.25) * mm, "end": v(15, -92.25) * mm});
            skLineSegment(sketch, "E93.MirrorCS", {"start": v(0, -74.25) * mm, "end": v(0, -104.25) * mm, "construction": true});
            skCircle(sketch, "E94.MirrorC", {"center": v(0, -104.25) * mm, "radius": 6 * mm});
            skSolve(sketch);
        }
        {
            var Q0;
            Q0 = qSketchRegion(id + "F16", true);
            extrude(context, id + "F17", {"entities" : qUnion([Q0]), "depth" : 3 * mm});
        }
    });
